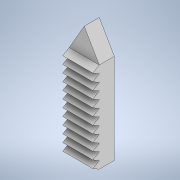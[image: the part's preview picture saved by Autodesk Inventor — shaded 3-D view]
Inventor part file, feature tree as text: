
AUTODESK INVENTOR PART (.ipt)
format: ipt  version: 2021 (Build 250183000, 183)  size: 156,160 bytes
history: native  units: mm
features: extrude x3, sketch x3, other x1
ambient origin geometry x8: Origin, YZ Plane, XZ Plane, XY Plane, X Axis, Y Axis, Z Axis, Center Point
bodies: Body1 (feature_tree)
feature tree (7):
  other  "Sólido1"
  extrude  "Extrusão1"  Depth=30.0mm
  extrude  "Extrusão2"  Depth=5.0mm TaperAngle=0.0deg
  extrude  "Extrusão3"  TaperAngle=150.0deg  [1 undecoded]
  sketch  "Esboço1"  dims[d0=30.0mm d3=30.0mm]
  sketch  "Esboço3"  dims[d4=10.0mm d5=5.0mm d6=0.0mm]
  sketch  "Esboço4"  dims[d10=2.5mm d11=150.0deg d12=2.5mm d13=2.5mm d14=2.5mm d15=2.5mm d16=150.0deg d17=10.0mm d18=0.0mm d19=5.0mm d20=1.0mm d21=0.0mm]
note: 1 required parameter value undecoded (feature->parameter linkage not recoverable at this tier; creation-order binding heuristic only, values carry confidence <= 0.55)
